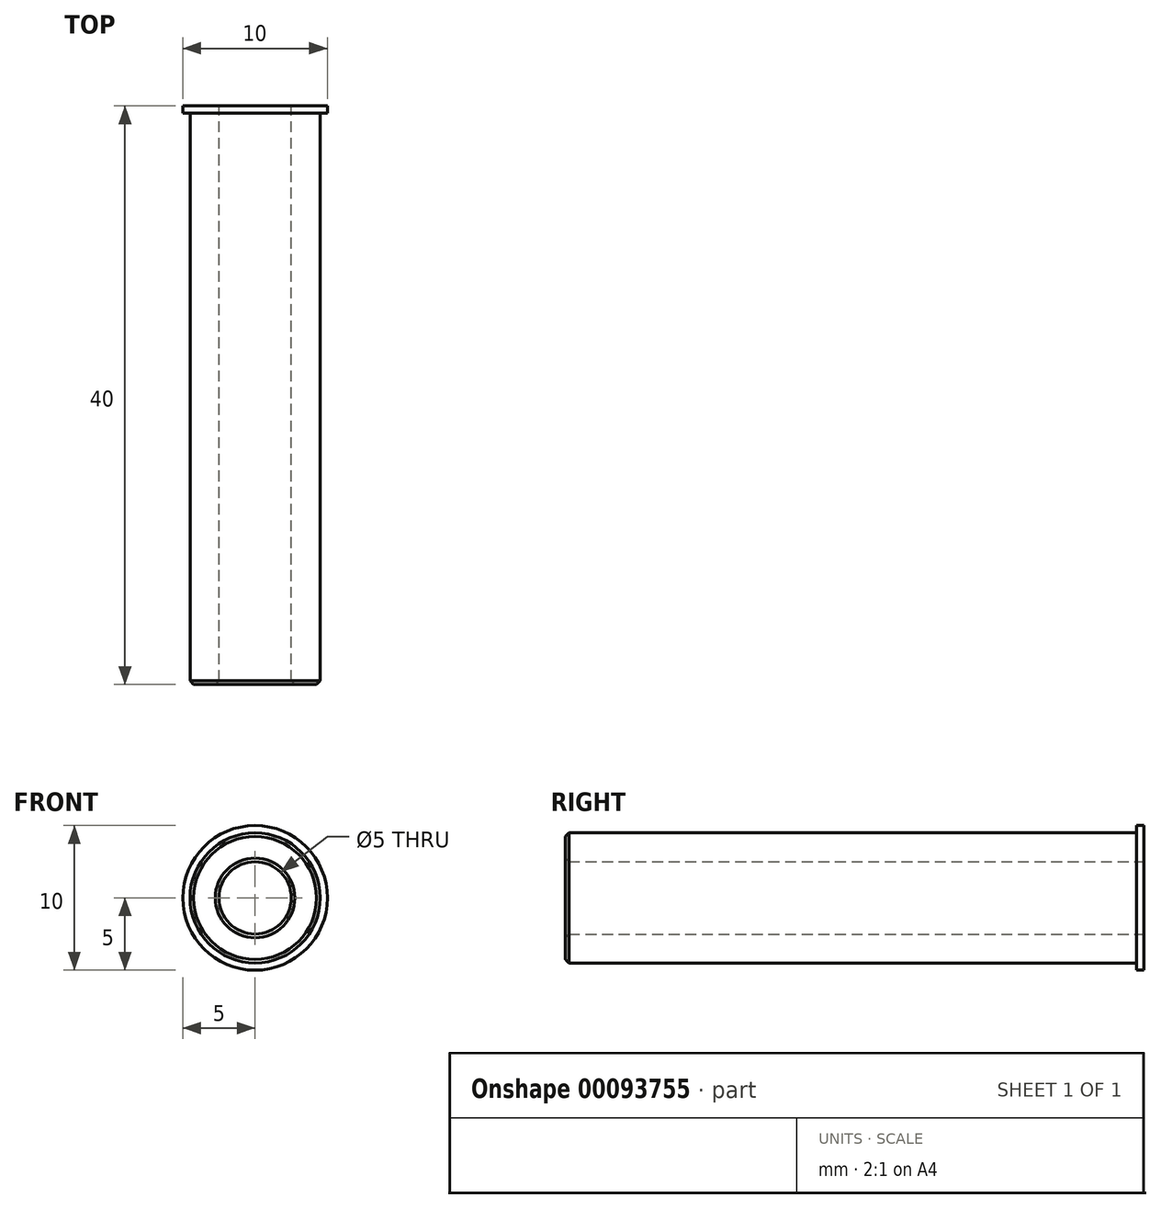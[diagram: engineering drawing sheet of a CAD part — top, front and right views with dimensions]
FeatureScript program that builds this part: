
annotation { "Feature Type Name" : "Feature", "Feature Type Description" : "" }
export const myFeature = defineFeature(function(context is Context, id is Id, definition is map)
    precondition{}
    {
        {
            var Q0;
            Q0=qCreatedBy(makeId("Front.planeOp"),FACE);
            var sketch = newSketch(context, id + "F0", { "sketchPlane" : qUnion([Q0])});
            skCircle(sketch, "E0", {"center": v(0, 0) * mm, "radius": 5 * mm});
            skCircle(sketch, "E1", {"center": v(0, 0) * mm, "radius": 2.5 * mm});
            skCircle(sketch, "E2", {"center": v(0, 0) * mm, "radius": 4.5 * mm});
            skSolve(sketch);
        }
        {
            var Q0;
            Q0=makeQuery(id+"F0.imprint","IMPRINT",FACE,{"disambiguationData":[TD([[makeQuery(id+"F0.imprint","IMPRINT",EDGE,{"derivedFrom":sQuery(id+"F0.wireOp",EDGE,"E1")}),-1.0]])]});
            extrude(context, id + "F1", {"entities" : qUnion([Q0]), "flatOperationType" : FlatOperationType.REMOVE, "offsetDistance" : 25 * mm, "depth" : 40 * mm, "domain" : OperationDomain.MODEL});
        }
        {
            var Q0;
            Q0=makeQuery(id+"F0.imprint","IMPRINT",FACE,{"disambiguationData":[TD([[makeQuery(id+"F0.imprint","IMPRINT",EDGE,{"derivedFrom":sQuery(id+"F0.wireOp",EDGE,"E0")}),1.0]])]});
            extrude(context, id + "F2", {"entities" : qUnion([Q0]), "operationType" : NewBodyOperationType.ADD, "flatOperationType" : FlatOperationType.REMOVE, "offsetDistance" : 25 * mm, "depth" : 0.5 * mm, "domain" : OperationDomain.MODEL});
        }
        {
            var Q0;
            Q0=makeQuery(id+"F1.opExtrude","CAP_FACE",FACE,{"disambiguationData":[OSD([sQuery(id+"F0.wireOp",EDGE,"E1"),sQuery(id+"F0.wireOp",EDGE,"E2")])],"isStart":false});
            chamfer(context, id + "F3", {"entities" : qUnion([Q0]), "width" : 0.25 * mm, "tangentPropagation" : true});
        }
        {
            var Q0;
            Q0=sQuery(id+"F0.wireOp",EDGE,"E1");
            extrude(context, id + "F4", {"bodyType" : ToolBodyType.SURFACE, "surfaceEntities" : qUnion([Q0]), "depth" : 4.5 * mm});
        }
    });
